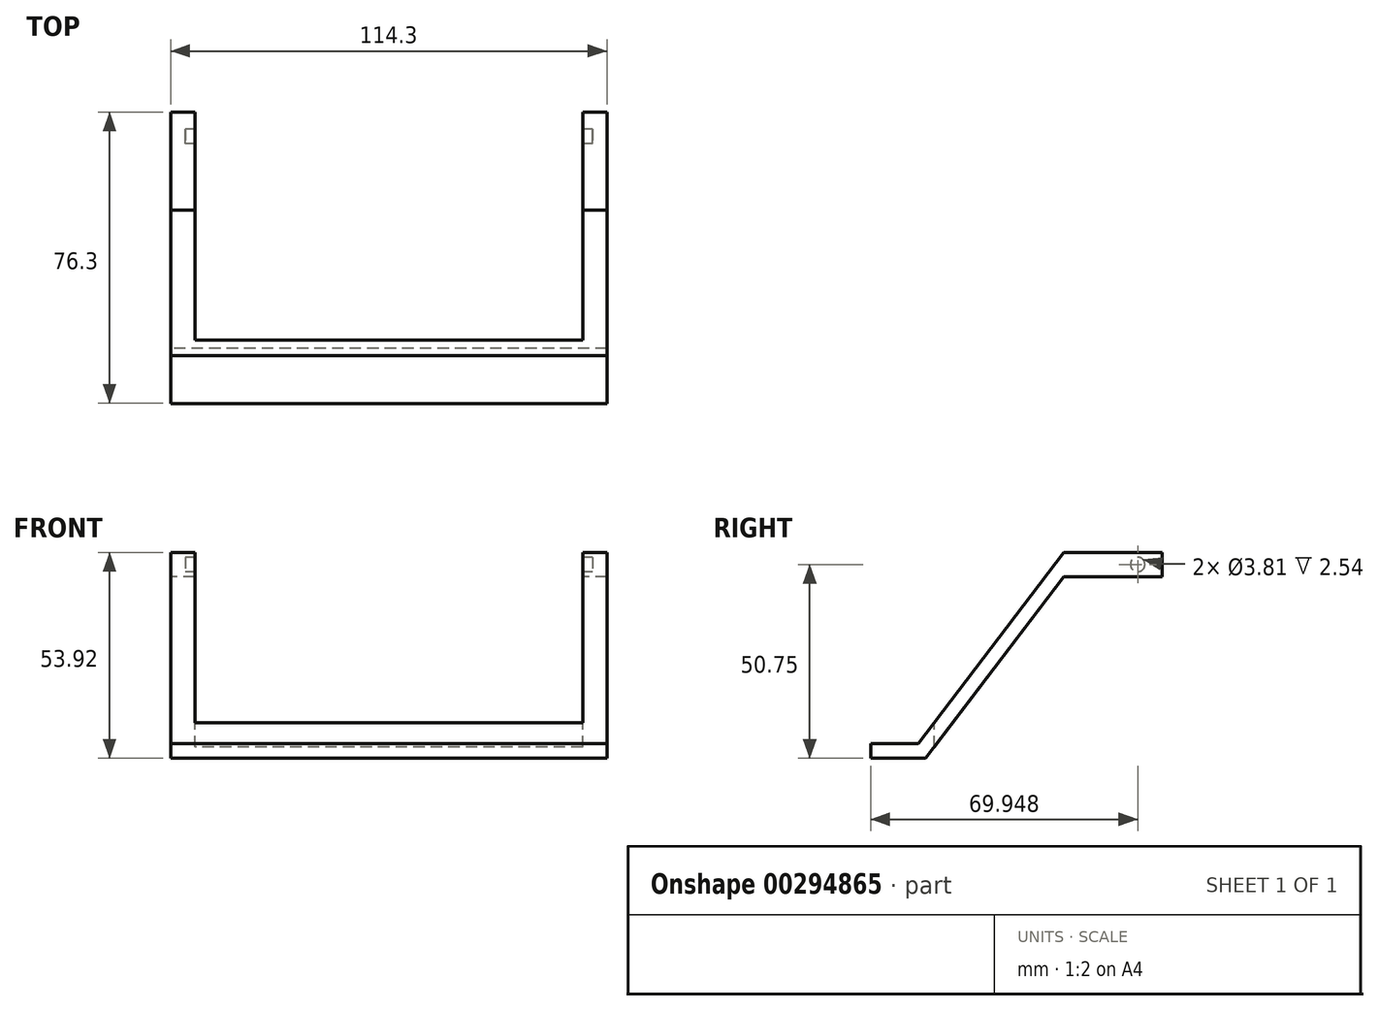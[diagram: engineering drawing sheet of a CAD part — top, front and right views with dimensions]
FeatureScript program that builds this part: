
annotation { "Feature Type Name" : "Feature", "Feature Type Description" : "" }
export const myFeature = defineFeature(function(context is Context, id is Id, definition is map)
    precondition{}
    {
        {
            var Q0;
            Q0=qCreatedBy(makeId("Right.planeOp"),FACE);
            var sketch = newSketch(context, id + "F0", { "sketchPlane" : qUnion([Q0])});
            skLineSegment(sketch, "E0.bottom", {"start": v(-50.8, 50.8) * mm, "end": v(50.8, 50.8) * mm});
            skLineSegment(sketch, "E0.top", {"start": v(-50.8, -50.8) * mm, "end": v(50.8, -50.8) * mm});
            skLineSegment(sketch, "E0.left", {"start": v(-50.8, 50.8) * mm, "end": v(-50.8, -50.8) * mm});
            skLineSegment(sketch, "E0.right", {"start": v(50.8, 50.8) * mm, "end": v(50.8, -50.8) * mm});
            skPoint(sketch, "E0.middle", {"position": v(0, 0) * mm});
            skLineSegment(sketch, "E1.bottom", {"start": v(4.38, 3.18) * mm, "end": v(-21.36, 3.18) * mm});
            skLineSegment(sketch, "E1.top", {"start": v(4.38, -3.18) * mm, "end": v(-21.36, -3.18) * mm});
            skLineSegment(sketch, "E1.left", {"start": v(4.38, 3.18) * mm, "end": v(4.38, -3.18) * mm});
            skLineSegment(sketch, "E1.right", {"start": v(-21.36, 3.18) * mm, "end": v(-21.36, -3.18) * mm});
            skLineSegment(sketch, "E2", {"start": v(-21.36, -3.17) * mm, "end": v(-57.5, -50.75) * mm});
            skLineSegment(sketch, "E3", {"start": v(-57.5, -50.75) * mm, "end": v(-62.32, -50.75) * mm});
            skLineSegment(sketch, "E4", {"start": v(-62.32, -50.75) * mm, "end": v(-21.36, 3.18) * mm});
            skLineSegment(sketch, "E5.bottom", {"start": v(-57.5, -50.75) * mm, "end": v(-71.92, -50.75) * mm});
            skLineSegment(sketch, "E5.top", {"start": v(-57.5, -46.94) * mm, "end": v(-71.92, -46.94) * mm});
            skLineSegment(sketch, "E5.left", {"start": v(-57.5, -50.75) * mm, "end": v(-57.5, -46.94) * mm});
            skLineSegment(sketch, "E5.right", {"start": v(-71.92, -50.75) * mm, "end": v(-71.92, -46.94) * mm});
            skLineSegment(sketch, "E6", {"start": v(-21.36, 0) * mm, "end": v(4.38, 0) * mm, "construction": true});
            skSolve(sketch);
        }
        {
            var Q0;
            Q0=makeQuery(id+"F0.imprint","IMPRINT",FACE,{"disambiguationData":[TD([[makeQuery(id+"F0.imprint","IMPRINT",EDGE,{"derivedFrom":sQuery(id+"F0.wireOp",EDGE,"E1.bottom")}),1.0]])]});
            var Q1;
            {var subQ5=sQuery(id+"F0.wireOp",EDGE,"E1.right");Q1=makeQuery(id+"F0.imprint","IMPRINT",FACE,{"disambiguationData":[TD([[makeQuery(id+"F0.imprint","IMPRINT",EDGE,{"derivedFrom":subQ5}),-1.0]])]});}
            var Q2;
            {var subQ5=sQuery(id+"F0.wireOp",EDGE,"E5.right");Q2=makeQuery(id+"F0.imprint","IMPRINT",FACE,{"disambiguationData":[TD([[makeQuery(id+"F0.imprint","IMPRINT",EDGE,{"derivedFrom":subQ5}),-1.0]])]});}
            var Q3;
            {var subQ0=sQuery(id+"F0.wireOp",EDGE,"E5.left");Q3=makeQuery(id+"F0.imprint","IMPRINT",FACE,{"disambiguationData":[TD([[makeQuery(id+"F0.imprint","IMPRINT",EDGE,{"derivedFrom":subQ0}),-1.0]])]});}
            var Q4;
            {var subQ5=sQuery(id+"F0.wireOp",EDGE,"E5.left");Q4=makeQuery(id+"F0.imprint","IMPRINT",FACE,{"disambiguationData":[TD([[makeQuery(id+"F0.imprint","IMPRINT",EDGE,{"derivedFrom":subQ5}),1.0]])]});}
            extrude(context, id + "F1", {"entities" : qUnion([Q0, Q1, Q2, Q3, Q4]), "depth" : 114.3 * mm});
        }
        {
            var Q0;
            Q0=makeQuery(id+"F1.opExtrude","SWEPT_FACE",FACE,{"disambiguationData":[OSD([sQuery(id+"F0.wireOp",EDGE,"E1.bottom")])]});
            var sketch = newSketch(context, id + "F2", { "sketchPlane" : qUnion([Q0])});
            skLineSegment(sketch, "E7.bottom", {"start": v(6.35, 4.38) * mm, "end": v(107.95, 4.38) * mm});
            skLineSegment(sketch, "E7.top", {"start": v(6.35, -55.31) * mm, "end": v(107.95, -55.31) * mm});
            skLineSegment(sketch, "E7.left", {"start": v(6.35, 4.38) * mm, "end": v(6.35, -55.31) * mm});
            skLineSegment(sketch, "E7.right", {"start": v(107.95, 4.38) * mm, "end": v(107.95, -55.31) * mm});
            skLineSegment(sketch, "E8", {"start": v(0, -8.5) * mm, "end": v(6.35, -8.5) * mm, "construction": true});
            skLineSegment(sketch, "E9", {"start": v(114.3, -8.5) * mm, "end": v(107.95, -8.5) * mm, "construction": true});
            skSolve(sketch);
        }
        {
            var Q0;
            {var subQ0=sQuery(id+"F2.wireOp",EDGE,"E7.bottom");Q0=makeQuery(id+"F2.imprint","IMPRINT",FACE,{"disambiguationData":[TD([[makeQuery(id+"F2.imprint","IMPRINT",EDGE,{"derivedFrom":subQ0}),1.0]])]});}
            var Q1;
            {var subQ0=sQuery(id+"F2.wireOp",EDGE,"E7.top");Q1=makeQuery(id+"F2.imprint","IMPRINT",FACE,{"disambiguationData":[TD([[makeQuery(id+"F2.imprint","IMPRINT",EDGE,{"derivedFrom":subQ0}),1.0]])]});}
            extrude(context, id + "F3", {"entities" : qUnion([Q0, Q1]), "operationType" : NewBodyOperationType.REMOVE, "oppositeDirection" : true, "depth" : 127 * mm});
        }
        {
            var Q0;
            Q0=makeQuery(id+"F3.boolean.opBoolean","COPY",FACE,{"derivedFrom":makeQuery(id+"F3.opExtrude","SWEPT_FACE",FACE,{"disambiguationData":[OSD([sQuery(id+"F2.wireOp",EDGE,"E7.right")])]})});
            cPlane(context, id + "F4", {"entities" : qUnion([Q0]), "cplaneType" : CPlaneType.OFFSET, "offset" : 50.8 * mm, "width" : 152.4 * mm, "height" : 152.4 * mm});
        }
        {
            var Q0;
            Q0=qCreatedBy(id+"F4.planeOp",FACE);
            var sketch = newSketch(context, id + "F5", { "sketchPlane" : qUnion([Q0])});
            skCircle(sketch, "E10", {"center": v(1.97, 0) * mm, "radius": 1.9 * mm});
            skSolve(sketch);
        }
        {
            var Q0;
            Q0=makeQuery(id+"F5.imprint","IMPRINT",FACE,{"disambiguationData":[TD([[makeQuery(id+"F5.imprint","IMPRINT",EDGE,{"derivedFrom":sQuery(id+"F5.wireOp",EDGE,"E10")}),1.0]])]});
            extrude(context, id + "F6", {"entities" : qUnion([Q0]), "operationType" : NewBodyOperationType.REMOVE, "oppositeDirection" : true, "depth" : 53.34 * mm, "hasSecondDirection" : true, "secondDirectionOppositeDirection" : false, "secondDirectionDepth" : 53.34 * mm});
        }
    });
